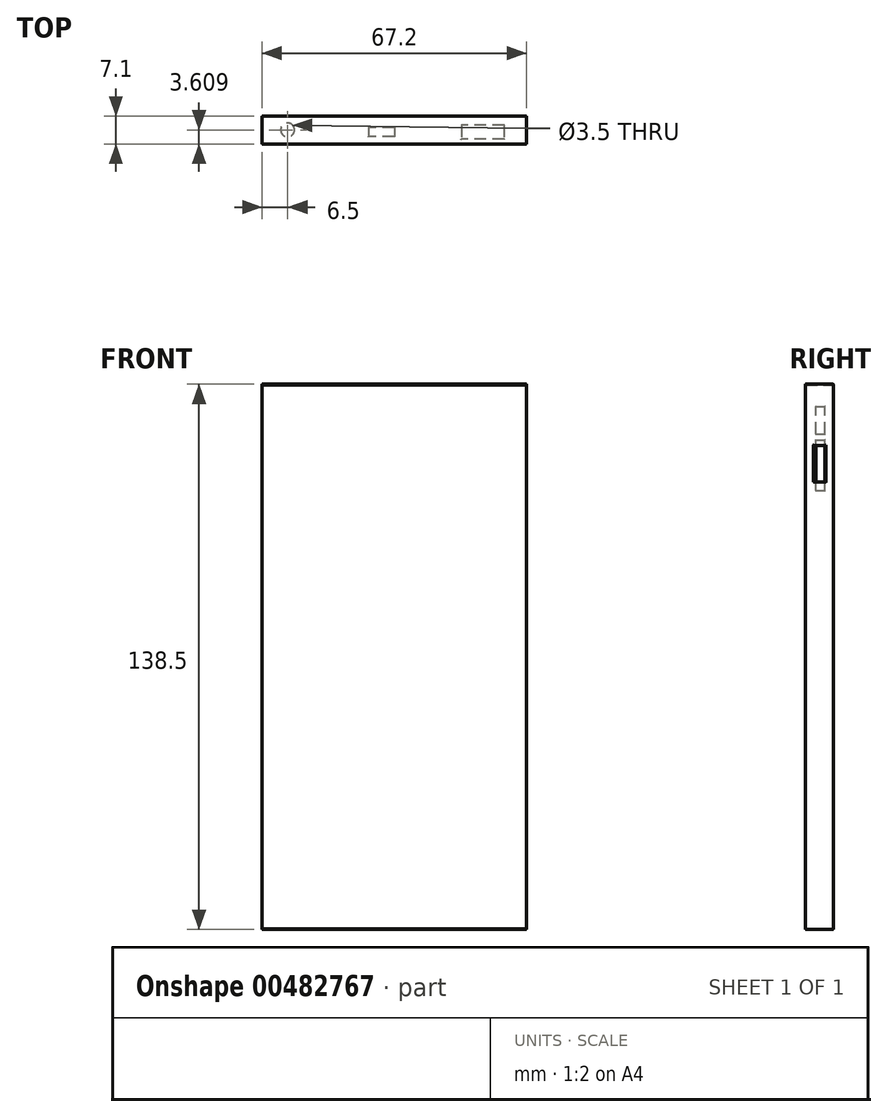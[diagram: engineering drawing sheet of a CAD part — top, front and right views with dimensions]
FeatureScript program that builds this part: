
annotation { "Feature Type Name" : "Feature", "Feature Type Description" : "" }
export const myFeature = defineFeature(function(context is Context, id is Id, definition is map)
    precondition{}
    {
        {
            var Q0;
            Q0=qCreatedBy(makeId("Front.planeOp"),FACE);
            var sketch = newSketch(context, id + "F0", { "sketchPlane" : qUnion([Q0])});
            skLineSegment(sketch, "E0.bottom", {"start": v(33.6, -69.25) * mm, "end": v(-33.6, -69.25) * mm});
            skLineSegment(sketch, "E0.top", {"start": v(33.6, 69.25) * mm, "end": v(-33.6, 69.25) * mm});
            skLineSegment(sketch, "E0.left", {"start": v(33.6, -69.25) * mm, "end": v(33.6, 69.25) * mm});
            skLineSegment(sketch, "E0.right", {"start": v(-33.6, -69.25) * mm, "end": v(-33.6, 69.25) * mm});
            skPoint(sketch, "E0.middle", {"position": v(0, 0) * mm});
            skLineSegment(sketch, "E1.bottom", {"start": v(33.55, -69.1) * mm, "end": v(-33.55, -69.1) * mm});
            skLineSegment(sketch, "E1.top", {"start": v(33.55, 69.1) * mm, "end": v(-33.55, 69.1) * mm});
            skLineSegment(sketch, "E1.left", {"start": v(33.55, -69.1) * mm, "end": v(33.55, 69.1) * mm});
            skLineSegment(sketch, "E1.right", {"start": v(-33.55, -69.1) * mm, "end": v(-33.55, 69.1) * mm});
            skSolve(sketch);
        }
        {
            var Q0;
            Q0 = qSketchRegion(id + "F0", true);
            extrude(context, id + "F1", {"entities" : qUnion([Q0]), "depth" : 7.1 * mm});
        }
        {
            var Q0;
            Q0=makeQuery(id+"F1.opExtrude","SWEPT_FACE",FACE,{"disambiguationData":[OSD([sQuery(id+"F0.wireOp",EDGE,"E0.bottom")])]});
            var sketch = newSketch(context, id + "F2", { "sketchPlane" : qUnion([Q0])});
            skCircle(sketch, "E2", {"center": v(-27.1, 3.5) * mm, "radius": 1.75 * mm});
            skLineSegment(sketch, "E3.bottom", {"start": v(0, 2.9) * mm, "end": v(-6.5, 2.9) * mm});
            skLineSegment(sketch, "E3.top", {"start": v(0, 5.24) * mm, "end": v(-6.5, 5.24) * mm});
            skLineSegment(sketch, "E3.left", {"start": v(0, 2.9) * mm, "end": v(0, 5.24) * mm});
            skLineSegment(sketch, "E3.right", {"start": v(-6.5, 2.9) * mm, "end": v(-6.5, 5.24) * mm});
            skPoint(sketch, "E3.middle", {"position": v(-3.25, 4.07) * mm});
            skLineSegment(sketch, "E4.bottom", {"start": v(27.93, 2.33) * mm, "end": v(17.07, 2.33) * mm});
            skLineSegment(sketch, "E4.top", {"start": v(27.93, 5.82) * mm, "end": v(17.07, 5.82) * mm});
            skLineSegment(sketch, "E4.left", {"start": v(27.93, 2.33) * mm, "end": v(27.93, 5.82) * mm});
            skLineSegment(sketch, "E4.right", {"start": v(17.07, 2.33) * mm, "end": v(17.07, 5.82) * mm});
            skPoint(sketch, "E4.middle", {"position": v(22.5, 4.07) * mm});
            skSolve(sketch);
        }
        {
            var Q0;
            Q0 = qSketchRegion(id + "F2", true);
            extrude(context, id + "F3", {"entities" : qUnion([Q0]), "operationType" : NewBodyOperationType.REMOVE, "oppositeDirection" : true, "depth" : 5 * mm});
        }
        {
            var Q0;
            Q0=makeQuery(id+"F1.opExtrude","SWEPT_FACE",FACE,{"disambiguationData":[OSD([sQuery(id+"F0.wireOp",EDGE,"E0.left")])]});
            var sketch = newSketch(context, id + "F4", { "sketchPlane" : qUnion([Q0])});
            skLineSegment(sketch, "E5.bottom", {"start": v(-1.94, 44.42) * mm, "end": v(-5.04, 44.42) * mm});
            skLineSegment(sketch, "E5.top", {"start": v(-1.94, 53.73) * mm, "end": v(-5.04, 53.73) * mm});
            skLineSegment(sketch, "E5.left", {"start": v(-1.94, 44.42) * mm, "end": v(-1.94, 53.73) * mm});
            skLineSegment(sketch, "E5.right", {"start": v(-5.04, 44.42) * mm, "end": v(-5.04, 53.73) * mm});
            skPoint(sketch, "E5.middle", {"position": v(-3.5, 49.07) * mm});
            skSolve(sketch);
        }
        {
            var Q0;
            Q0 = qSketchRegion(id + "F4", true);
            extrude(context, id + "F5", {"entities" : qUnion([Q0]), "operationType" : NewBodyOperationType.REMOVE, "oppositeDirection" : true, "depth" : 5 * mm});
        }
        {
            var Q0;
            Q0=makeQuery(id+"F1.opExtrude","SWEPT_FACE",FACE,{"disambiguationData":[OSD([sQuery(id+"F0.wireOp",EDGE,"E0.right")])]});
            var sketch = newSketch(context, id + "F6", { "sketchPlane" : qUnion([Q0])});
            skLineSegment(sketch, "E6.bottom", {"start": v(4.46, 56.64) * mm, "end": v(2.13, 56.64) * mm});
            skLineSegment(sketch, "E6.top", {"start": v(4.46, 63.62) * mm, "end": v(2.13, 63.62) * mm});
            skLineSegment(sketch, "E6.left", {"start": v(4.46, 56.64) * mm, "end": v(4.46, 63.62) * mm});
            skLineSegment(sketch, "E6.right", {"start": v(2.13, 56.64) * mm, "end": v(2.13, 63.62) * mm});
            skPoint(sketch, "E6.middle", {"position": v(3.3, 60.13) * mm});
            skLineSegment(sketch, "E7.bottom", {"start": v(4.46, 42.28) * mm, "end": v(2.13, 42.28) * mm});
            skLineSegment(sketch, "E7.top", {"start": v(4.46, 55.09) * mm, "end": v(2.13, 55.09) * mm});
            skLineSegment(sketch, "E7.left", {"start": v(4.46, 42.28) * mm, "end": v(4.46, 55.09) * mm});
            skLineSegment(sketch, "E7.right", {"start": v(2.13, 42.28) * mm, "end": v(2.13, 55.09) * mm});
            skPoint(sketch, "E7.middle", {"position": v(3.3, 48.69) * mm});
            skSolve(sketch);
        }
        {
            var Q0;
            Q0 = qSketchRegion(id + "F6", true);
            extrude(context, id + "F7", {"entities" : qUnion([Q0]), "operationType" : NewBodyOperationType.REMOVE, "oppositeDirection" : true, "depth" : 5 * mm});
        }
        {
            var Q0;
            Q0=makeQuery(id+"F1.opExtrude","SWEPT_FACE",FACE,{"disambiguationData":[OSD([sQuery(id+"F0.wireOp",EDGE,"E0.top")])]});
            var Q1;
            Q1=makeQuery(id+"F1.opExtrude","SWEPT_FACE",FACE,{"disambiguationData":[OSD([sQuery(id+"F0.wireOp",EDGE,"E0.left")])]});
            var Q2;
            Q2=makeQuery(id+"F1.opExtrude","SWEPT_FACE",FACE,{"disambiguationData":[OSD([sQuery(id+"F0.wireOp",EDGE,"E0.right")])]});
            var Q3;
            Q3=makeQuery(id+"F1.opExtrude","SWEPT_FACE",FACE,{"disambiguationData":[OSD([sQuery(id+"F0.wireOp",EDGE,"E0.bottom")])]});
            fillet(context, id + "F8", {"entities" : qUnion([Q0, Q1, Q2, Q3]), "radius" : 0.1 * mm, "tangentPropagation" : true, "allowEdgeOverflow" : false});
        }
    });
